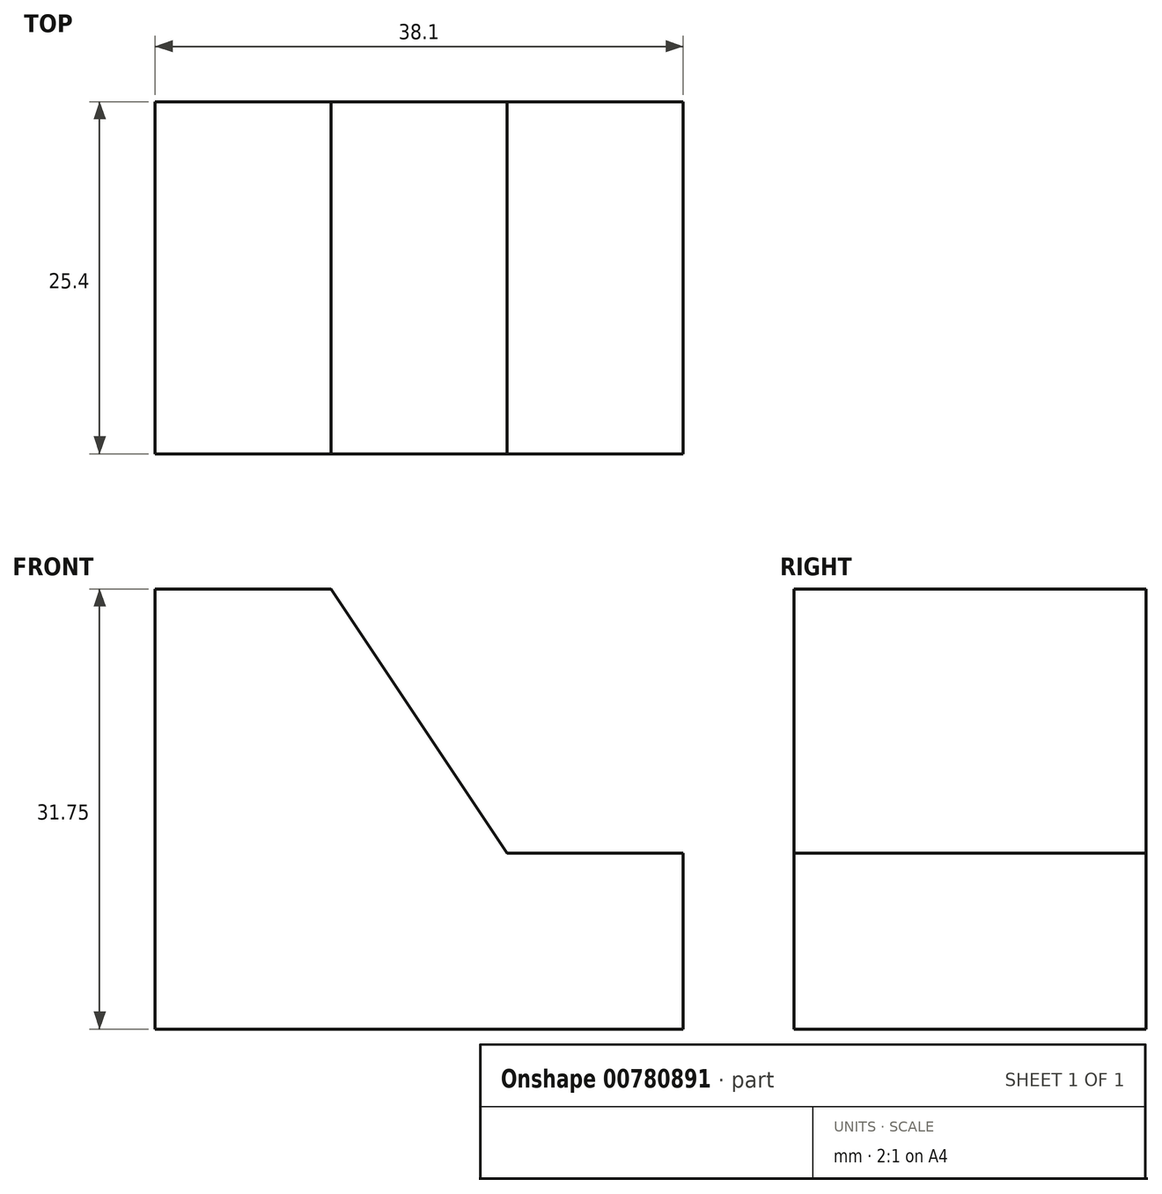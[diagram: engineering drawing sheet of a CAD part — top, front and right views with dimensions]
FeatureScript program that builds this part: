
annotation { "Feature Type Name" : "Feature", "Feature Type Description" : "" }
export const myFeature = defineFeature(function(context is Context, id is Id, definition is map)
    precondition{}
    {
        {
            var Q0;
            Q0=qCreatedBy(makeId("Front.planeOp"),FACE);
            var sketch = newSketch(context, id + "F0", { "sketchPlane" : qUnion([Q0])});
            skLineSegment(sketch, "E0", {"start": v(0, 0) * mm, "end": v(38.1, 0) * mm});
            skLineSegment(sketch, "E1", {"start": v(38.1, 12.7) * mm, "end": v(38.1, 0) * mm});
            skLineSegment(sketch, "E2", {"start": v(25.4, 12.7) * mm, "end": v(38.1, 12.7) * mm});
            skLineSegment(sketch, "E3", {"start": v(0, 0) * mm, "end": v(0, 31.75) * mm});
            skLineSegment(sketch, "E4", {"start": v(0, 31.75) * mm, "end": v(12.7, 31.75) * mm});
            skLineSegment(sketch, "E5", {"start": v(12.7, 31.75) * mm, "end": v(25.4, 12.7) * mm});
            skSolve(sketch);
        }
        {
            var Q0;
            Q0 = qSketchRegion(id + "F0", true);
            extrude(context, id + "F1", {"entities" : qUnion([Q0]), "depth" : 25.4 * mm, "offsetDistance" : 25.4 * mm});
        }
    });
